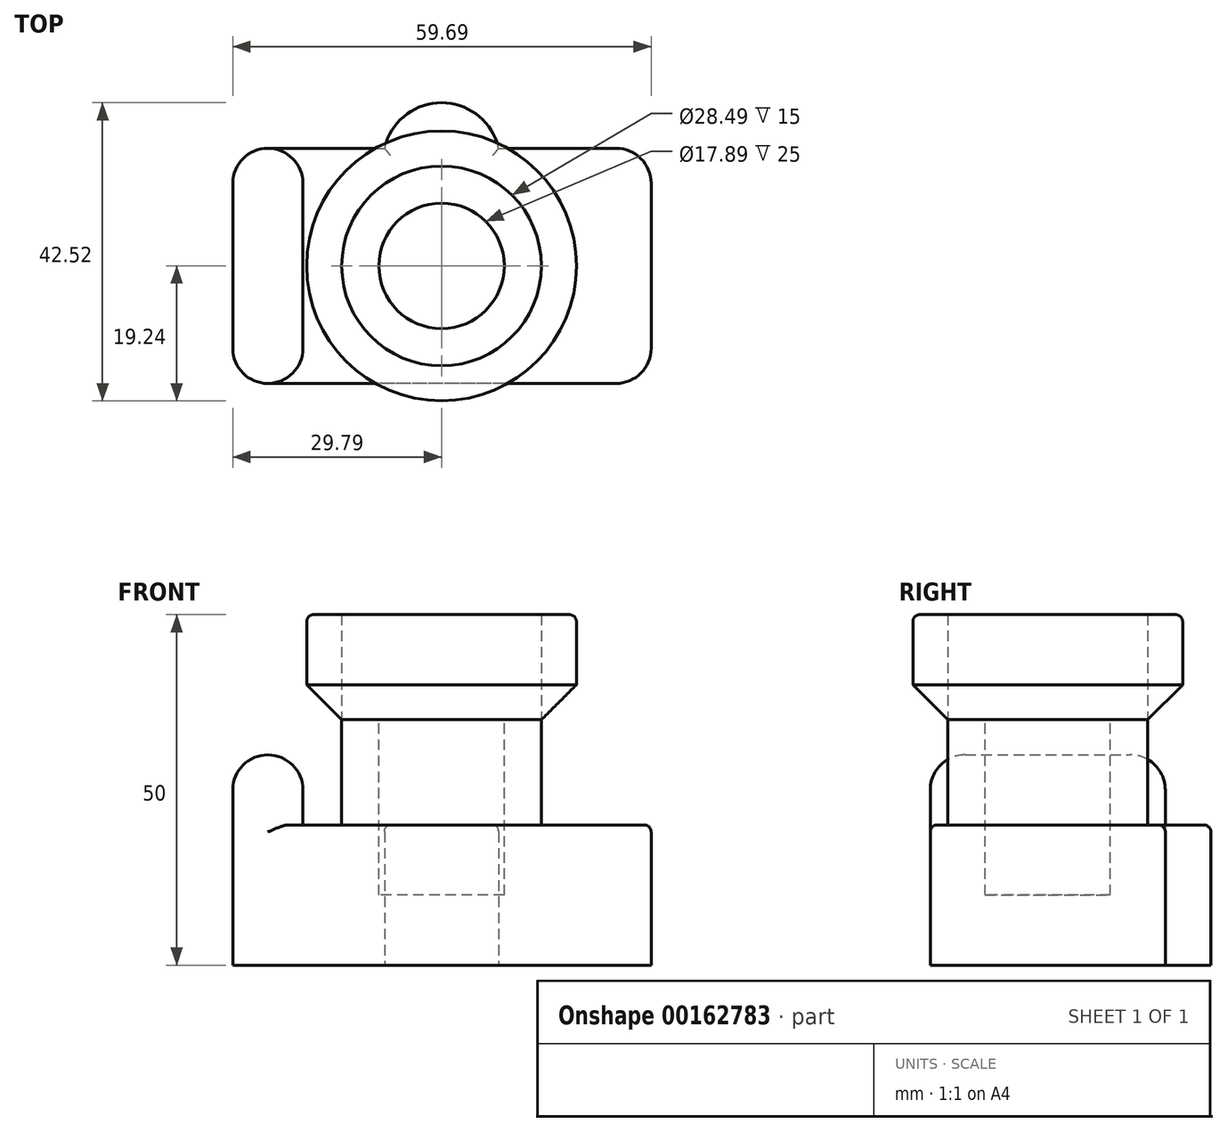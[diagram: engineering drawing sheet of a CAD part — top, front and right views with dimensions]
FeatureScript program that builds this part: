
annotation { "Feature Type Name" : "Feature", "Feature Type Description" : "" }
export const myFeature = defineFeature(function(context is Context, id is Id, definition is map)
    precondition{}
    {
        {
            var Q0;
            Q0=qCreatedBy(makeId("Top.planeOp"),FACE);
            var sketch = newSketch(context, id + "F0", { "sketchPlane" : qUnion([Q0])});
            skLineSegment(sketch, "E0", {"start": v(-29.79, -11.77) * mm, "end": v(-29.79, 11.77) * mm});
            skLineSegment(sketch, "E1", {"start": v(-24.79, 16.77) * mm, "end": v(-8.14, 16.77) * mm});
            skArc(sketch, "E2", {"start": v(8.14, 16.77) * mm, "mid": v(0, 23.28) * mm, "end": v(-8.14, 16.77) * mm});
            skLineSegment(sketch, "E3", {"start": v(8.14, 16.77) * mm, "end": v(24.9, 16.77) * mm});
            skLineSegment(sketch, "E4", {"start": v(29.9, 11.77) * mm, "end": v(29.9, -11.77) * mm});
            skLineSegment(sketch, "E5", {"start": v(24.9, -16.77) * mm, "end": v(-24.79, -16.77) * mm});
            skPoint(sketch, "E6.visualSharp", {"position": v(-29.79, 16.77) * mm});
            skArc(sketch, "E6.filletArc", {"start": v(-24.79, 16.77) * mm, "mid": v(-28.32, 15.3) * mm, "end": v(-29.79, 11.77) * mm});
            skPoint(sketch, "E7.visualSharp", {"position": v(29.9, 16.77) * mm});
            skArc(sketch, "E7.filletArc", {"start": v(29.9, 11.77) * mm, "mid": v(28.43, 15.3) * mm, "end": v(24.9, 16.77) * mm});
            skPoint(sketch, "E8.visualSharp", {"position": v(29.9, -16.77) * mm});
            skArc(sketch, "E8.filletArc", {"start": v(24.9, -16.77) * mm, "mid": v(28.43, -15.3) * mm, "end": v(29.9, -11.77) * mm});
            skPoint(sketch, "E9.visualSharp", {"position": v(-29.79, -16.77) * mm});
            skArc(sketch, "E9.filletArc", {"start": v(-29.79, -11.77) * mm, "mid": v(-28.32, -15.3) * mm, "end": v(-24.79, -16.77) * mm});
            skSolve(sketch);
        }
        {
            var Q0;
            Q0=makeQuery(id+"F0.imprint","IMPRINT",FACE,{"disambiguationData":[TD([[makeQuery(id+"F0.imprint","IMPRINT",EDGE,{"derivedFrom":sQuery(id+"F0.wireOp",EDGE,"E0")}),-1.0]])]});
            extrude(context, id + "F1", {"entities" : qUnion([Q0]), "depth" : 20 * mm});
        }
        {
            var Q0;
            Q0=makeQuery(id+"F1.opExtrude","CAP_FACE",FACE,{"disambiguationData":[OSD([sQuery(id+"F0.wireOp",EDGE,"E0"),sQuery(id+"F0.wireOp",EDGE,"E1"),sQuery(id+"F0.wireOp",EDGE,"E2"),sQuery(id+"F0.wireOp",EDGE,"E3"),sQuery(id+"F0.wireOp",EDGE,"E4"),sQuery(id+"F0.wireOp",EDGE,"E5"),sQuery(id+"F0.wireOp",EDGE,"E6.filletArc"),sQuery(id+"F0.wireOp",EDGE,"E7.filletArc"),sQuery(id+"F0.wireOp",EDGE,"E8.filletArc"),sQuery(id+"F0.wireOp",EDGE,"E9.filletArc")])],"isStart":false});
            var sketch = newSketch(context, id + "F2", { "sketchPlane" : qUnion([Q0])});
            skArc(sketch, "E10.0", {"start": v(-24.79, 16.77) * mm, "mid": v(-28.32, 15.3) * mm, "end": v(-29.79, 11.77) * mm});
            skLineSegment(sketch, "E11.0", {"start": v(-29.79, -11.77) * mm, "end": v(-29.79, 11.77) * mm});
            skArc(sketch, "E12.0", {"start": v(-29.79, -11.77) * mm, "mid": v(-28.32, -15.3) * mm, "end": v(-24.79, -16.77) * mm});
            skLineSegment(sketch, "E13", {"start": v(-24.79, 16.77) * mm, "end": v(-24.79, 11.77) * mm, "construction": true});
            skArc(sketch, "E14.MirrorCS", {"start": v(-24.79, 16.77) * mm, "mid": v(-21.25, 15.3) * mm, "end": v(-19.79, 11.77) * mm});
            skLineSegment(sketch, "E15.MirrorCS", {"start": v(-19.79, -11.77) * mm, "end": v(-19.79, 11.77) * mm});
            skArc(sketch, "E16.MirrorCS", {"start": v(-19.79, -11.77) * mm, "mid": v(-21.25, -15.3) * mm, "end": v(-24.79, -16.77) * mm});
            skSolve(sketch);
        }
        {
            var Q0;
            Q0=makeQuery(id+"F2.imprint","IMPRINT",FACE,{"disambiguationData":[TD([[makeQuery(id+"F2.imprint","IMPRINT",EDGE,{"derivedFrom":sQuery(id+"F2.wireOp",EDGE,"E10.0")}),1.0]])]});
            extrude(context, id + "F3", {"entities" : qUnion([Q0]), "operationType" : NewBodyOperationType.ADD, "depth" : 10 * mm});
        }
        {
            var Q0;
            Q0=makeQuery(id+"F3.opExtrude","CAP_EDGE",EDGE,{"disambiguationData":[OSD([sQuery(id+"F2.wireOp",EDGE,"E10.0"),sQuery(id+"F2.wireOp",EDGE,"E14.MirrorCS")])],"isStart":false});
            var Q1;
            Q1=makeQuery(id+"F3.opExtrude","CAP_EDGE",EDGE,{"disambiguationData":[OSD([sQuery(id+"F2.wireOp",EDGE,"E11.0")])],"isStart":false});
            var Q2;
            Q2=makeQuery(id+"F3.opExtrude","CAP_EDGE",EDGE,{"disambiguationData":[OSD([sQuery(id+"F2.wireOp",EDGE,"E15.MirrorCS")])],"isStart":false});
            var Q3;
            Q3=makeQuery(id+"F3.opExtrude","CAP_EDGE",EDGE,{"disambiguationData":[OSD([sQuery(id+"F2.wireOp",EDGE,"E12.0"),sQuery(id+"F2.wireOp",EDGE,"E16.MirrorCS")])],"isStart":false});
            fillet(context, id + "F4", {"entities" : qUnion([Q0, Q1, Q2, Q3]), "radius" : 5 * mm, "tangentPropagation" : true, "allowEdgeOverflow" : false});
        }
        {
            var Q0;
            Q0=makeQuery(id+"F1.opExtrude","CAP_EDGE",EDGE,{"disambiguationData":[OSD([sQuery(id+"F0.wireOp",EDGE,"E1")])],"isStart":false});
            var Q1;
            Q1=makeQuery(id+"F1.opExtrude","CAP_EDGE",EDGE,{"disambiguationData":[OSD([sQuery(id+"F0.wireOp",EDGE,"E2")])],"isStart":false});
            var Q2;
            Q2=makeQuery(id+"F1.opExtrude","CAP_EDGE",EDGE,{"disambiguationData":[OSD([sQuery(id+"F0.wireOp",EDGE,"E3")])],"isStart":false});
            var Q3;
            Q3=makeQuery(id+"F1.opExtrude","CAP_EDGE",EDGE,{"disambiguationData":[OSD([sQuery(id+"F0.wireOp",EDGE,"E7.filletArc")])],"isStart":false});
            var Q4;
            Q4=makeQuery(id+"F1.opExtrude","CAP_EDGE",EDGE,{"disambiguationData":[OSD([sQuery(id+"F0.wireOp",EDGE,"E4")])],"isStart":false});
            var Q5;
            Q5=makeQuery(id+"F1.opExtrude","CAP_EDGE",EDGE,{"disambiguationData":[OSD([sQuery(id+"F0.wireOp",EDGE,"E8.filletArc")])],"isStart":false});
            var Q6;
            Q6=makeQuery(id+"F1.opExtrude","CAP_EDGE",EDGE,{"disambiguationData":[OSD([sQuery(id+"F0.wireOp",EDGE,"E5")])],"isStart":false});
            fillet(context, id + "F5", {"entities" : qUnion([Q0, Q1, Q2, Q3, Q4, Q5, Q6]), "radius" : 1 * mm, "tangentPropagation" : true, "allowEdgeOverflow" : false});
        }
        {
            var Q0;
            Q0=makeQuery(id+"F1.opExtrude","CAP_FACE",FACE,{"disambiguationData":[OSD([sQuery(id+"F0.wireOp",EDGE,"E0"),sQuery(id+"F0.wireOp",EDGE,"E1"),sQuery(id+"F0.wireOp",EDGE,"E2"),sQuery(id+"F0.wireOp",EDGE,"E3"),sQuery(id+"F0.wireOp",EDGE,"E4"),sQuery(id+"F0.wireOp",EDGE,"E5"),sQuery(id+"F0.wireOp",EDGE,"E6.filletArc"),sQuery(id+"F0.wireOp",EDGE,"E7.filletArc"),sQuery(id+"F0.wireOp",EDGE,"E8.filletArc"),sQuery(id+"F0.wireOp",EDGE,"E9.filletArc")])],"isStart":false});
            var sketch = newSketch(context, id + "F6", { "sketchPlane" : qUnion([Q0])});
            skLineSegment(sketch, "E17.0", {"start": v(-21.79, -15.77) * mm, "end": v(24.9, -15.77) * mm});
            skCircle(sketch, "E18", {"center": v(0, 0) * mm, "radius": 14.24 * mm});
            skSolve(sketch);
        }
        {
            var Q0;
            Q0=makeQuery(id+"F6.imprint","IMPRINT",FACE,{"disambiguationData":[TD([[makeQuery(id+"F6.imprint","IMPRINT",EDGE,{"derivedFrom":sQuery(id+"F6.wireOp",EDGE,"E18")}),1.0]])]});
            extrude(context, id + "F7", {"entities" : qUnion([Q0]), "operationType" : NewBodyOperationType.ADD, "depth" : 15 * mm});
        }
        {
            var Q0;
            Q0=makeQuery(id+"F7.opExtrude","CAP_FACE",FACE,{"disambiguationData":[OSD([sQuery(id+"F6.wireOp",EDGE,"E18")])],"isStart":false});
            var sketch = newSketch(context, id + "F8", { "sketchPlane" : qUnion([Q0])});
            skCircle(sketch, "E19.0", {"center": v(0, 0) * mm, "radius": 14.24 * mm});
            skCircle(sketch, "E20.0", {"center": v(0, 0) * mm, "radius": 19.24 * mm});
            skSolve(sketch);
        }
        {
            var Q0;
            Q0=makeQuery(id+"F8.imprint","IMPRINT",FACE,{"disambiguationData":[TD([[makeQuery(id+"F8.imprint","IMPRINT",EDGE,{"derivedFrom":sQuery(id+"F8.wireOp",EDGE,"E19.0")}),-1.0]])]});
            extrude(context, id + "F9", {"entities" : qUnion([Q0]), "depth" : 15 * mm});
        }
        {
            var Q0;
            Q0=makeQuery(id+"F9.opExtrude","CAP_EDGE",EDGE,{"disambiguationData":[OSD([sQuery(id+"F8.wireOp",EDGE,"E20.0")])],"isStart":true});
            chamfer(context, id + "F10", {"entities" : qUnion([Q0]), "width" : 5 * mm, "tangentPropagation" : true});
        }
        {
            var Q0;
            Q0=makeQuery(id+"F7.opExtrude","CAP_FACE",FACE,{"disambiguationData":[OSD([sQuery(id+"F6.wireOp",EDGE,"E18")])],"isStart":false});
            var sketch = newSketch(context, id + "F11", { "sketchPlane" : qUnion([Q0])});
            skCircle(sketch, "E21", {"center": v(0, 0) * mm, "radius": 8.95 * mm});
            skSolve(sketch);
        }
        {
            var Q0;
            Q0=makeQuery(id+"F11.imprint","IMPRINT",FACE,{"disambiguationData":[TD([[makeQuery(id+"F11.imprint","IMPRINT",EDGE,{"derivedFrom":sQuery(id+"F11.wireOp",EDGE,"E21")}),1.0]])]});
            extrude(context, id + "F12", {"entities" : qUnion([Q0]), "operationType" : NewBodyOperationType.REMOVE, "oppositeDirection" : true, "depth" : 25 * mm});
        }
        {
            var Q0;
            Q0=makeQuery(id+"F9.opExtrude","CAP_EDGE",EDGE,{"disambiguationData":[OSD([sQuery(id+"F8.wireOp",EDGE,"E20.0")])],"isStart":false});
            fillet(context, id + "F13", {"entities" : qUnion([Q0]), "radius" : 1 * mm, "tangentPropagation" : true, "allowEdgeOverflow" : false});
        }
    });
